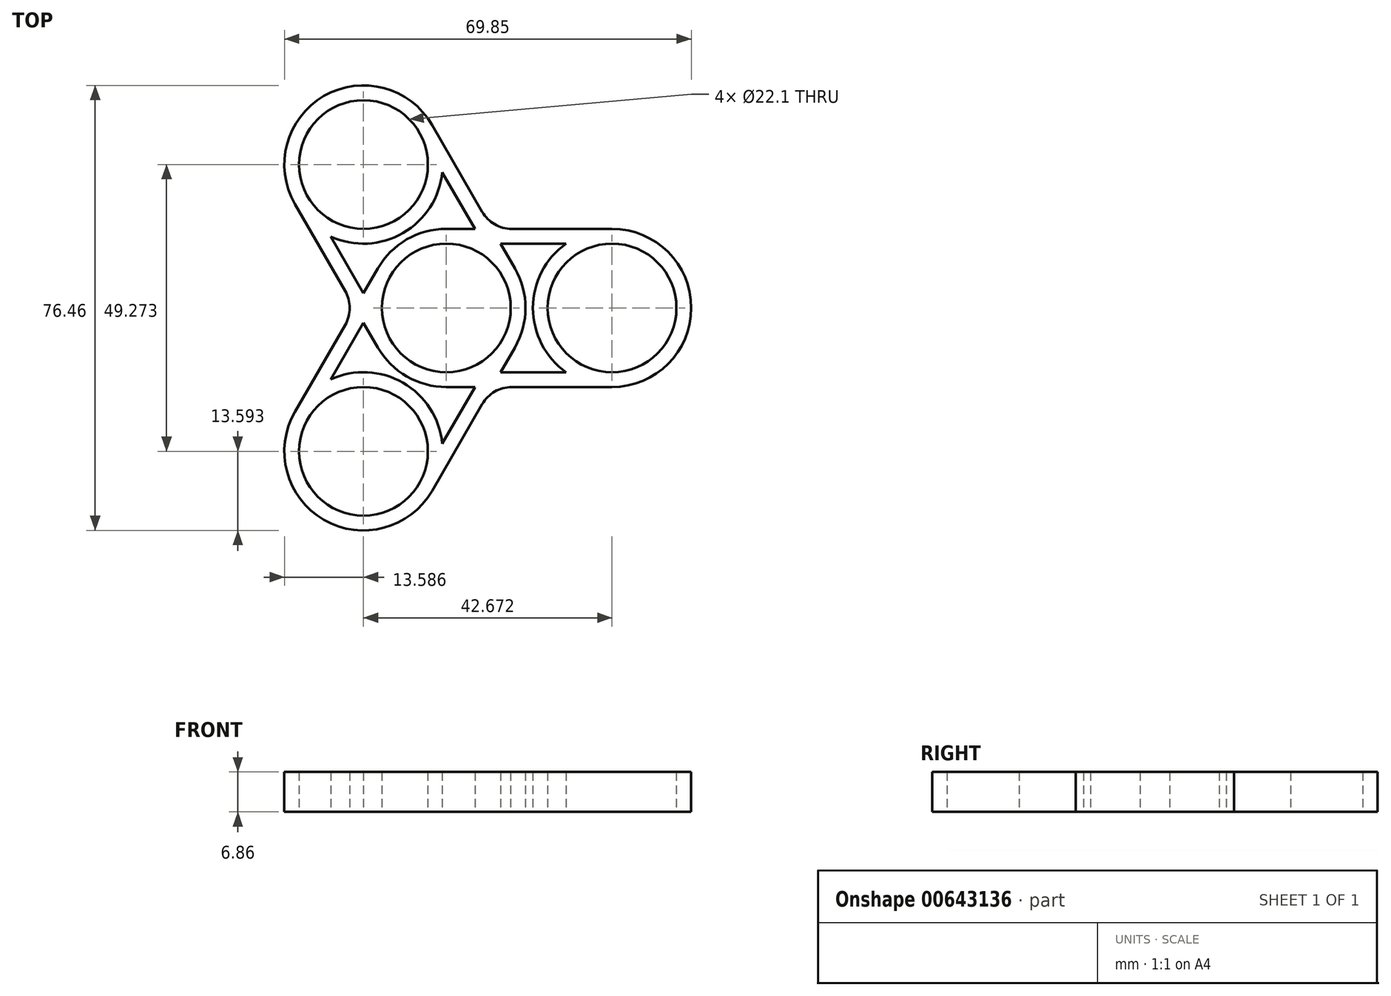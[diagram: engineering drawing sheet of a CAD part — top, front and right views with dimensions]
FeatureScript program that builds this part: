
annotation { "Feature Type Name" : "Feature", "Feature Type Description" : "" }
export const myFeature = defineFeature(function(context is Context, id is Id, definition is map)
    precondition{}
    {
        {
            var Q0;
            Q0=qCreatedBy(makeId("Top.planeOp"),FACE);
            var sketch = newSketch(context, id + "F0", { "sketchPlane" : qUnion([Q0])});
            skCircle(sketch, "E0", {"center": v(0, 0) * mm, "radius": 11.05 * mm});
            skCircle(sketch, "E1", {"center": v(0, 0) * mm, "radius": 13.59 * mm});
            skCircle(sketch, "E2", {"center": v(28.45, 0) * mm, "radius": 11.05 * mm});
            skCircle(sketch, "E3", {"center": v(28.45, 0) * mm, "radius": 13.59 * mm});
            skLineSegment(sketch, "E4", {"start": v(0, 13.59) * mm, "end": v(28.45, 13.59) * mm});
            skLineSegment(sketch, "E5", {"start": v(0, 11.05) * mm, "end": v(28.45, 11.05) * mm});
            skLineSegment(sketch, "E6", {"start": v(0, -11.05) * mm, "end": v(28.45, -11.05) * mm});
            skLineSegment(sketch, "E7", {"start": v(0, -13.59) * mm, "end": v(28.45, -13.59) * mm});
            skCircle(sketch, "E8.1.0", {"center": v(-14.22, 24.64) * mm, "radius": 11.05 * mm});
            skCircle(sketch, "E8.1.1", {"center": v(-14.22, 24.64) * mm, "radius": 13.59 * mm});
            skLineSegment(sketch, "E8.1.2", {"start": v(-9.57, -5.52) * mm, "end": v(-23.8, 19.11) * mm});
            skLineSegment(sketch, "E8.1.3", {"start": v(-11.77, -6.8) * mm, "end": v(-26, 17.84) * mm});
            skLineSegment(sketch, "E8.1.4", {"start": v(9.57, 5.52) * mm, "end": v(-4.66, 30.16) * mm});
            skLineSegment(sketch, "E8.1.5", {"start": v(11.77, 6.8) * mm, "end": v(-2.46, 31.43) * mm});
            skCircle(sketch, "E8.2.0", {"center": v(-14.22, -24.64) * mm, "radius": 11.05 * mm});
            skCircle(sketch, "E8.2.1", {"center": v(-14.22, -24.64) * mm, "radius": 13.59 * mm});
            skLineSegment(sketch, "E8.2.2", {"start": v(9.57, -5.52) * mm, "end": v(-4.66, -30.16) * mm});
            skLineSegment(sketch, "E8.2.3", {"start": v(11.77, -6.8) * mm, "end": v(-2.46, -31.43) * mm});
            skLineSegment(sketch, "E8.2.4", {"start": v(-9.57, 5.52) * mm, "end": v(-23.8, -19.11) * mm});
            skLineSegment(sketch, "E8.2.5", {"start": v(-11.77, 6.8) * mm, "end": v(-26, -17.84) * mm});
            skArc(sketch, "E9", {"start": v(6.15, 16.52) * mm, "mid": v(8.3, 14.37) * mm, "end": v(11.23, 13.59) * mm});
            skArc(sketch, "E10", {"start": v(11.23, -13.59) * mm, "mid": v(8.3, -14.38) * mm, "end": v(6.15, -16.52) * mm});
            skArc(sketch, "E11", {"start": v(-17.38, -2.93) * mm, "mid": v(-16.6, 0) * mm, "end": v(-17.38, 2.93) * mm});
            skSolve(sketch);
        }
        {
            var Q0;
            Q0 = qSketchRegion(id + "F0", true);
            var Q1;
            {var subQ1=sQuery(id+"F0.wireOp",EDGE,"E1");var subQ5=sQuery(id+"F0.wireOp",EDGE,"E8.1.2");var subQ6=makeQuery(id+"F0.imprint","INTERSECT",VERTEX,{"derivedFrom":[subQ1,subQ5]});Q1=makeQuery(id+"F0.imprint","IMPRINT",FACE,{"disambiguationData":[TD([[makeQuery(id+"F0.imprint","IMPRINT",EDGE,{"disambiguationData":[TD([[subQ6,-1.0]])],"derivedFrom":subQ1}),-1.0]])]});}
            var Q2;
            {var subQ0=sQuery(id+"F0.wireOp",EDGE,"E8.1.2");var subQ1=sQuery(id+"F0.wireOp",EDGE,"E1");var subQ2=makeQuery(id+"F0.imprint","INTERSECT",VERTEX,{"derivedFrom":[subQ1,subQ0]});Q2=makeQuery(id+"F0.imprint","IMPRINT",FACE,{"disambiguationData":[TD([[makeQuery(id+"F0.imprint","IMPRINT",EDGE,{"disambiguationData":[TD([[subQ2,-1.0]])],"derivedFrom":subQ1}),1.0]])]});}
            var Q3;
            {var subQ7=sQuery(id+"F0.wireOp",EDGE,"E5");var subQ8=sQuery(id+"F0.wireOp",EDGE,"E0");var subQ9=makeQuery(id+"F0.imprint","INTERSECT",VERTEX,{"derivedFrom":[subQ8,subQ7]});Q3=makeQuery(id+"F0.imprint","IMPRINT",FACE,{"disambiguationData":[TD([[makeQuery(id+"F0.imprint","IMPRINT",EDGE,{"disambiguationData":[TD([[subQ9,-1.0]])],"derivedFrom":subQ8}),-1.0]])]});}
            var Q4;
            {var subQ0=sQuery(id+"F0.wireOp",EDGE,"E8.1.2");var subQ1=sQuery(id+"F0.wireOp",EDGE,"E0");var subQ2=makeQuery(id+"F0.imprint","INTERSECT",VERTEX,{"derivedFrom":[subQ1,subQ0]});Q4=makeQuery(id+"F0.imprint","IMPRINT",FACE,{"disambiguationData":[TD([[makeQuery(id+"F0.imprint","IMPRINT",EDGE,{"disambiguationData":[TD([[subQ2,1.0]])],"derivedFrom":subQ1}),-1.0]])]});}
            var Q5;
            {var subQ0=sQuery(id+"F0.wireOp",EDGE,"E8.2.5");var subQ1=sQuery(id+"F0.wireOp",EDGE,"E1");var subQ2=makeQuery(id+"F0.imprint","INTERSECT",VERTEX,{"derivedFrom":[subQ1,subQ0]});Q5=makeQuery(id+"F0.imprint","IMPRINT",FACE,{"disambiguationData":[TD([[makeQuery(id+"F0.imprint","IMPRINT",EDGE,{"disambiguationData":[TD([[subQ2,-1.0]])],"derivedFrom":subQ1}),-1.0]])]});}
            var Q6;
            {var subQ0=sQuery(id+"F0.wireOp",EDGE,"E8.1.3");var subQ1=sQuery(id+"F0.wireOp",EDGE,"E1");var subQ2=makeQuery(id+"F0.imprint","INTERSECT",VERTEX,{"derivedFrom":[subQ1,subQ0]});Q6=makeQuery(id+"F0.imprint","IMPRINT",FACE,{"disambiguationData":[TD([[makeQuery(id+"F0.imprint","IMPRINT",EDGE,{"disambiguationData":[TD([[subQ2,1.0]])],"derivedFrom":subQ1}),-1.0]])]});}
            var Q7;
            {var subQ4=sQuery(id+"F0.wireOp",EDGE,"E6");var subQ5=sQuery(id+"F0.wireOp",EDGE,"E0");var subQ6=makeQuery(id+"F0.imprint","INTERSECT",VERTEX,{"derivedFrom":[subQ5,subQ4]});Q7=makeQuery(id+"F0.imprint","IMPRINT",FACE,{"disambiguationData":[TD([[makeQuery(id+"F0.imprint","IMPRINT",EDGE,{"disambiguationData":[TD([[subQ6,1.0]])],"derivedFrom":subQ5}),-1.0]])]});}
            var Q8;
            {var subQ0=sQuery(id+"F0.wireOp",EDGE,"E6");var subQ1=sQuery(id+"F0.wireOp",EDGE,"E0");var subQ2=makeQuery(id+"F0.imprint","INTERSECT",VERTEX,{"derivedFrom":[subQ1,subQ0]});Q8=makeQuery(id+"F0.imprint","IMPRINT",FACE,{"disambiguationData":[TD([[makeQuery(id+"F0.imprint","IMPRINT",EDGE,{"disambiguationData":[TD([[subQ2,-1.0]])],"derivedFrom":subQ1}),-1.0]])]});}
            var Q9;
            {var subQ0=sQuery(id+"F0.wireOp",EDGE,"E8.2.2");var subQ1=sQuery(id+"F0.wireOp",EDGE,"E1");var subQ2=makeQuery(id+"F0.imprint","INTERSECT",VERTEX,{"derivedFrom":[subQ1,subQ0]});Q9=makeQuery(id+"F0.imprint","IMPRINT",FACE,{"disambiguationData":[TD([[makeQuery(id+"F0.imprint","IMPRINT",EDGE,{"disambiguationData":[TD([[subQ2,-1.0]])],"derivedFrom":subQ1}),1.0]])]});}
            var Q10;
            {var subQ0=sQuery(id+"F0.wireOp",EDGE,"E8.2.2");var subQ1=sQuery(id+"F0.wireOp",EDGE,"E1");var subQ2=makeQuery(id+"F0.imprint","INTERSECT",VERTEX,{"derivedFrom":[subQ1,subQ0]});Q10=makeQuery(id+"F0.imprint","IMPRINT",FACE,{"disambiguationData":[TD([[makeQuery(id+"F0.imprint","IMPRINT",EDGE,{"disambiguationData":[TD([[subQ2,-1.0]])],"derivedFrom":subQ1}),-1.0]])]});}
            var Q11;
            {var subQ0=sQuery(id+"F0.wireOp",EDGE,"E7");var subQ1=sQuery(id+"F0.wireOp",EDGE,"E1");var subQ2=makeQuery(id+"F0.imprint","INTERSECT",VERTEX,{"derivedFrom":[subQ1,subQ0]});Q11=makeQuery(id+"F0.imprint","IMPRINT",FACE,{"disambiguationData":[TD([[makeQuery(id+"F0.imprint","IMPRINT",EDGE,{"disambiguationData":[TD([[subQ2,-1.0]])],"derivedFrom":subQ1}),-1.0]])]});}
            var Q12;
            {var subQ0=sQuery(id+"F0.wireOp",EDGE,"E8.2.3");var subQ1=sQuery(id+"F0.wireOp",EDGE,"E1");var subQ2=makeQuery(id+"F0.imprint","INTERSECT",VERTEX,{"derivedFrom":[subQ1,subQ0]});Q12=makeQuery(id+"F0.imprint","IMPRINT",FACE,{"disambiguationData":[TD([[makeQuery(id+"F0.imprint","IMPRINT",EDGE,{"disambiguationData":[TD([[subQ2,1.0]])],"derivedFrom":subQ1}),-1.0]])]});}
            var Q13;
            {var subQ6=sQuery(id+"F0.wireOp",EDGE,"E0");var subQ11=sQuery(id+"F0.wireOp",EDGE,"E8.1.4");var subQ12=makeQuery(id+"F0.imprint","INTERSECT",VERTEX,{"derivedFrom":[subQ6,subQ11]});Q13=makeQuery(id+"F0.imprint","IMPRINT",FACE,{"disambiguationData":[TD([[makeQuery(id+"F0.imprint","IMPRINT",EDGE,{"disambiguationData":[TD([[subQ12,1.0]])],"derivedFrom":subQ6}),-1.0]])]});}
            var Q14;
            {var subQ1=sQuery(id+"F0.wireOp",EDGE,"E1");var subQ5=sQuery(id+"F0.wireOp",EDGE,"E5");var subQ6=makeQuery(id+"F0.imprint","INTERSECT",VERTEX,{"derivedFrom":[subQ1,subQ5]});Q14=makeQuery(id+"F0.imprint","IMPRINT",FACE,{"disambiguationData":[TD([[makeQuery(id+"F0.imprint","IMPRINT",EDGE,{"disambiguationData":[TD([[subQ6,-1.0]])],"derivedFrom":subQ1}),-1.0]])]});}
            var Q15;
            {var subQ0=sQuery(id+"F0.wireOp",EDGE,"E5");var subQ1=sQuery(id+"F0.wireOp",EDGE,"E1");var subQ2=makeQuery(id+"F0.imprint","INTERSECT",VERTEX,{"derivedFrom":[subQ1,subQ0]});Q15=makeQuery(id+"F0.imprint","IMPRINT",FACE,{"disambiguationData":[TD([[makeQuery(id+"F0.imprint","IMPRINT",EDGE,{"disambiguationData":[TD([[subQ2,-1.0]])],"derivedFrom":subQ1}),1.0]])]});}
            var Q16;
            {var subQ0=sQuery(id+"F0.wireOp",EDGE,"E5");var subQ1=sQuery(id+"F0.wireOp",EDGE,"E0");var subQ2=makeQuery(id+"F0.imprint","INTERSECT",VERTEX,{"derivedFrom":[subQ1,subQ0]});Q16=makeQuery(id+"F0.imprint","IMPRINT",FACE,{"disambiguationData":[TD([[makeQuery(id+"F0.imprint","IMPRINT",EDGE,{"disambiguationData":[TD([[subQ2,1.0]])],"derivedFrom":subQ1}),-1.0]])]});}
            var Q17;
            {var subQ0=sQuery(id+"F0.wireOp",EDGE,"E4");var subQ1=sQuery(id+"F0.wireOp",EDGE,"E1");var subQ2=makeQuery(id+"F0.imprint","INTERSECT",VERTEX,{"derivedFrom":[subQ1,subQ0]});Q17=makeQuery(id+"F0.imprint","IMPRINT",FACE,{"disambiguationData":[TD([[makeQuery(id+"F0.imprint","IMPRINT",EDGE,{"disambiguationData":[TD([[subQ2,1.0]])],"derivedFrom":subQ1}),-1.0]])]});}
            var Q18;
            {var subQ0=sQuery(id+"F0.wireOp",EDGE,"E8.1.5");var subQ1=sQuery(id+"F0.wireOp",EDGE,"E1");var subQ2=makeQuery(id+"F0.imprint","INTERSECT",VERTEX,{"derivedFrom":[subQ1,subQ0]});Q18=makeQuery(id+"F0.imprint","IMPRINT",FACE,{"disambiguationData":[TD([[makeQuery(id+"F0.imprint","IMPRINT",EDGE,{"disambiguationData":[TD([[subQ2,-1.0]])],"derivedFrom":subQ1}),-1.0]])]});}
            var Q19;
            {var subQ0=sQuery(id+"F0.wireOp",EDGE,"E5");var subQ1=sQuery(id+"F0.wireOp",EDGE,"E2");var subQ2=makeQuery(id+"F0.imprint","INTERSECT",VERTEX,{"derivedFrom":[subQ1,subQ0]});Q19=makeQuery(id+"F0.imprint","IMPRINT",FACE,{"disambiguationData":[TD([[makeQuery(id+"F0.imprint","IMPRINT",EDGE,{"disambiguationData":[TD([[subQ2,-1.0]])],"derivedFrom":subQ1}),-1.0]])]});}
            var Q20;
            {var subQ0=sQuery(id+"F0.wireOp",EDGE,"E8.1.2");var subQ1=sQuery(id+"F0.wireOp",EDGE,"E8.1.0");var subQ2=makeQuery(id+"F0.imprint","INTERSECT",VERTEX,{"derivedFrom":[subQ1,subQ0]});Q20=makeQuery(id+"F0.imprint","IMPRINT",FACE,{"disambiguationData":[TD([[makeQuery(id+"F0.imprint","IMPRINT",EDGE,{"disambiguationData":[TD([[subQ2,-1.0]])],"derivedFrom":subQ1}),-1.0]])]});}
            var Q21;
            {var subQ0=sQuery(id+"F0.wireOp",EDGE,"E8.2.2");var subQ1=sQuery(id+"F0.wireOp",EDGE,"E8.2.0");var subQ2=makeQuery(id+"F0.imprint","INTERSECT",VERTEX,{"derivedFrom":[subQ1,subQ0]});Q21=makeQuery(id+"F0.imprint","IMPRINT",FACE,{"disambiguationData":[TD([[makeQuery(id+"F0.imprint","IMPRINT",EDGE,{"disambiguationData":[TD([[subQ2,-1.0]])],"derivedFrom":subQ1}),-1.0]])]});}
            extrude(context, id + "F1", {"entities" : qUnion([Q0, Q1, Q2, Q3, Q4, Q5, Q6, Q7, Q8, Q9, Q10, Q11, Q12, Q13, Q14, Q15, Q16, Q17, Q18, Q19, Q20, Q21]), "depth" : 6.86 * mm, "offsetDistance" : 25.4 * mm});
        }
    });
